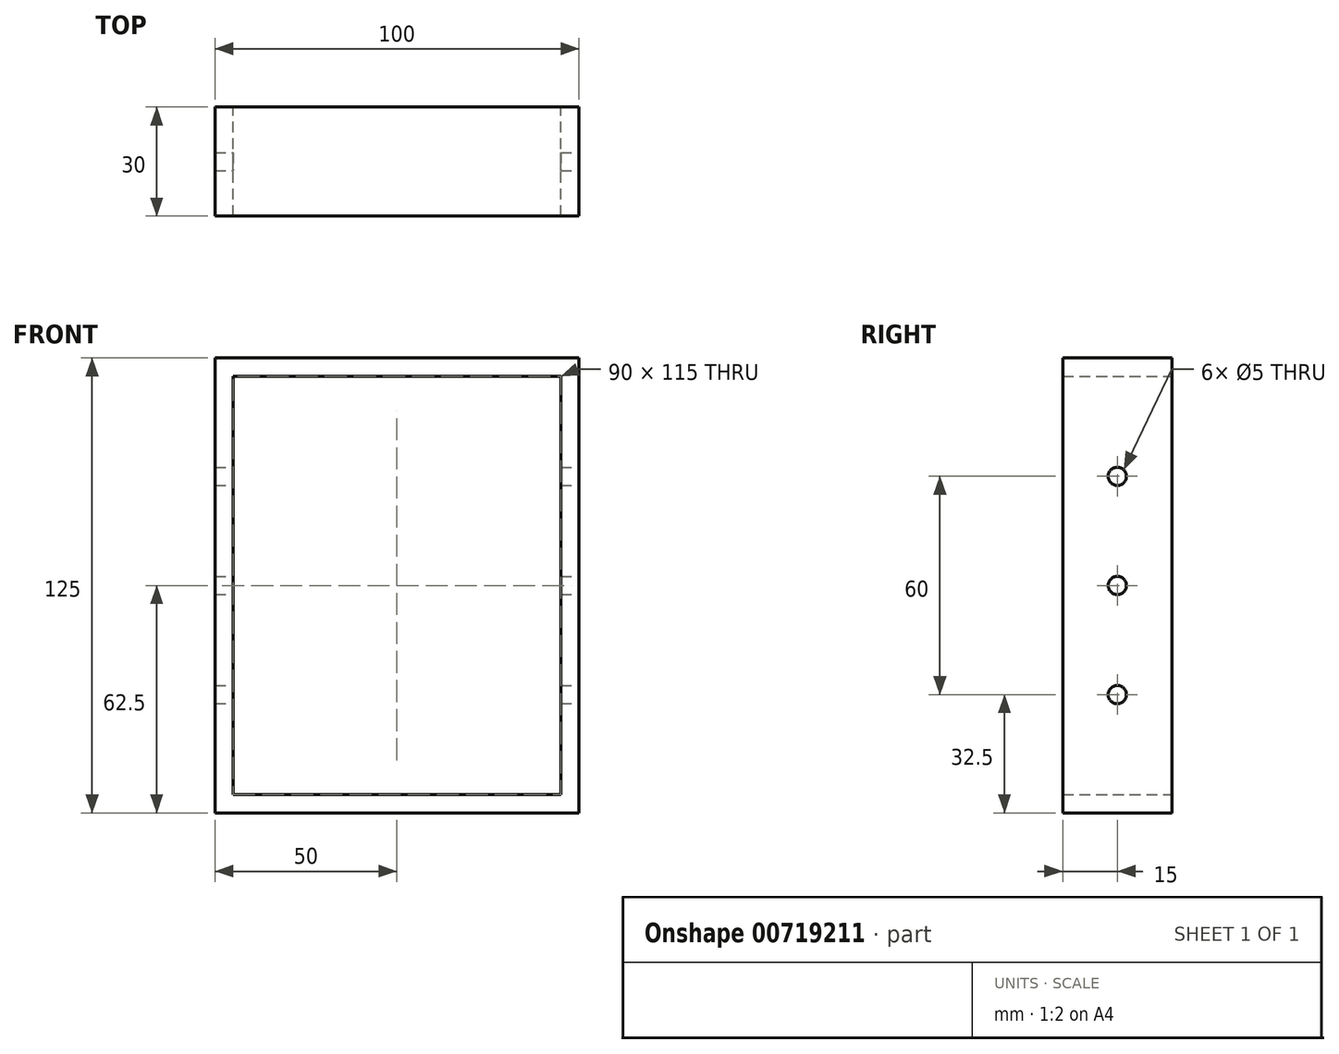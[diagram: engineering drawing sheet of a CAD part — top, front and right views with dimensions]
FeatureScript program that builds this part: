
annotation { "Feature Type Name" : "Feature", "Feature Type Description" : "" }
export const myFeature = defineFeature(function(context is Context, id is Id, definition is map)
    precondition{}
    {
        {
            var Q0;
            Q0=qCreatedBy(makeId("Front.planeOp"),FACE);
            var sketch = newSketch(context, id + "F0", { "sketchPlane" : qUnion([Q0])});
            skLineSegment(sketch, "E0.bottom", {"start": v(-50, 62.5) * mm, "end": v(50, 62.5) * mm});
            skLineSegment(sketch, "E0.top", {"start": v(-50, -62.5) * mm, "end": v(50, -62.5) * mm});
            skLineSegment(sketch, "E0.left", {"start": v(-50, 62.5) * mm, "end": v(-50, -62.5) * mm});
            skLineSegment(sketch, "E0.right", {"start": v(50, 62.5) * mm, "end": v(50, -62.5) * mm});
            skPoint(sketch, "E0.middle", {"position": v(0, 0) * mm});
            skLineSegment(sketch, "E1.bottom", {"start": v(-45, 57.5) * mm, "end": v(45, 57.5) * mm});
            skLineSegment(sketch, "E1.top", {"start": v(-45, -57.5) * mm, "end": v(45, -57.5) * mm});
            skLineSegment(sketch, "E1.left", {"start": v(-45, 57.5) * mm, "end": v(-45, -57.5) * mm});
            skLineSegment(sketch, "E1.right", {"start": v(45, 57.5) * mm, "end": v(45, -57.5) * mm});
            skSolve(sketch);
        }
        {
            var Q0;
            Q0=makeQuery(id+"F0.imprint","IMPRINT",FACE,{"disambiguationData":[TD([[makeQuery(id+"F0.imprint","IMPRINT",EDGE,{"derivedFrom":sQuery(id+"F0.wireOp",EDGE,"E0.bottom")}),-1.0]])]});
            extrude(context, id + "F1", {"entities" : qUnion([Q0]), "depth" : 30 * mm, "offsetDistance" : 25 * mm});
        }
        {
            var Q0;
            Q0=makeQuery(id+"F1.opExtrude","SWEPT_FACE",FACE,{"disambiguationData":[OSD([sQuery(id+"F0.wireOp",EDGE,"E0.left")])]});
            var sketch = newSketch(context, id + "F2", { "sketchPlane" : qUnion([Q0])});
            skCircle(sketch, "E2", {"center": v(15, 30) * mm, "radius": 2.5 * mm});
            skCircle(sketch, "E3", {"center": v(15, 0) * mm, "radius": 2.5 * mm});
            skCircle(sketch, "E4", {"center": v(15, -30) * mm, "radius": 2.5 * mm});
            skSolve(sketch);
        }
        {
            var Q0;
            Q0=makeQuery(id+"F2.imprint","IMPRINT",FACE,{"disambiguationData":[TD([[makeQuery(id+"F2.imprint","IMPRINT",EDGE,{"derivedFrom":sQuery(id+"F2.wireOp",EDGE,"E2")}),1.0]])]});
            var Q1;
            Q1=makeQuery(id+"F2.imprint","IMPRINT",FACE,{"disambiguationData":[TD([[makeQuery(id+"F2.imprint","IMPRINT",EDGE,{"derivedFrom":sQuery(id+"F2.wireOp",EDGE,"E3")}),1.0]])]});
            var Q2;
            Q2=makeQuery(id+"F2.imprint","IMPRINT",FACE,{"disambiguationData":[TD([[makeQuery(id+"F2.imprint","IMPRINT",EDGE,{"derivedFrom":sQuery(id+"F2.wireOp",EDGE,"E4")}),1.0]])]});
            extrude(context, id + "F3", {"entities" : qUnion([Q0, Q1, Q2]), "operationType" : NewBodyOperationType.REMOVE, "depth" : 200 * mm, "offsetDistance" : 25 * mm, "hasSecondDirection" : true, "secondDirectionOppositeDirection" : true, "secondDirectionDepth" : 200 * mm});
        }
    });
